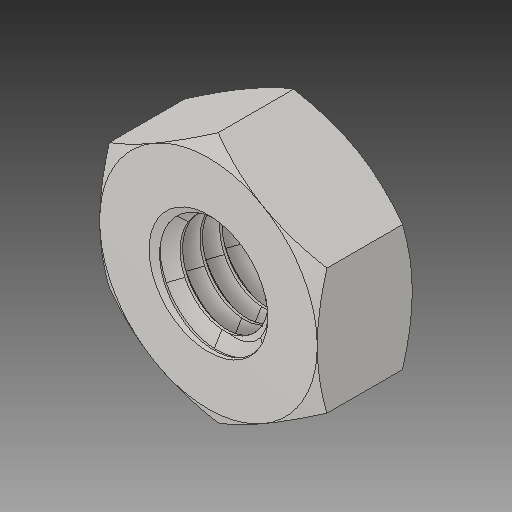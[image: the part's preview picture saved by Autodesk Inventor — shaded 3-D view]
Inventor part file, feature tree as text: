
AUTODESK INVENTOR PART (.ipt)
format: ipt  version: 2019 (Build 230136000, 136)  size: 441,856 bytes
history: imported  units: mm
features: imported_body x1
ambient origin geometry x8: Origin, YZ Plane, XZ Plane, XY Plane, X Axis, Y Axis, Z Axis, Center Point
bodies: Solide1 (imported_parasolid), Body1 (imported_parasolid)
feature tree (1):
  imported_body  NMx_Import_Brep_tag  [imported B-rep: ~3 faces, bbox_mm=None]
